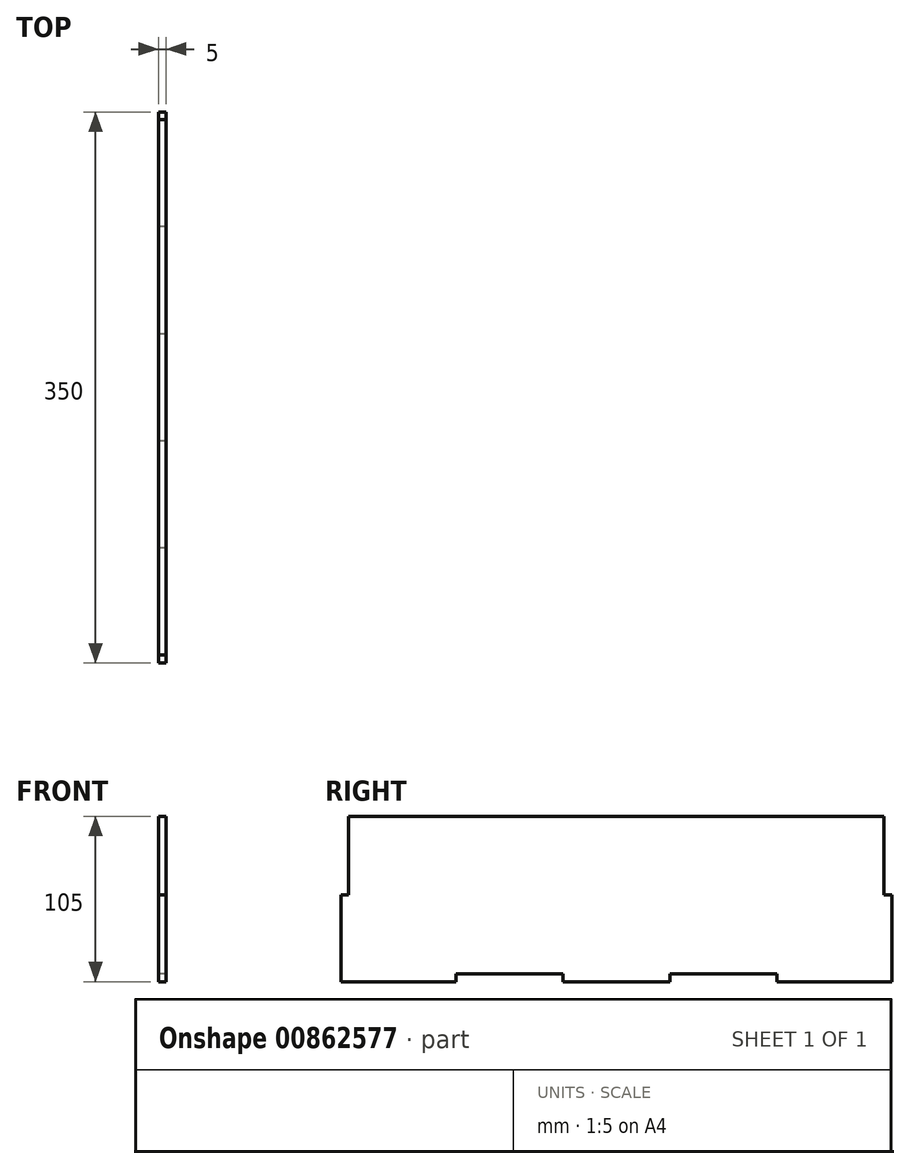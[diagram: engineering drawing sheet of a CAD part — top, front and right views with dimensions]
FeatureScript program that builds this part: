
annotation { "Feature Type Name" : "Feature", "Feature Type Description" : "" }
export const myFeature = defineFeature(function(context is Context, id is Id, definition is map)
    precondition{}
    {
        {
            var Q0;
            Q0=qCreatedBy(makeId("Right.planeOp"),FACE);
            var sketch = newSketch(context, id + "F0", { "sketchPlane" : qUnion([Q0])});
            skLineSegment(sketch, "E0.bottom", {"start": v(175, -50) * mm, "end": v(-175, -50) * mm});
            skLineSegment(sketch, "E0.top", {"start": v(170, 50) * mm, "end": v(-170, 50) * mm});
            skLineSegment(sketch, "E0.left", {"start": v(175, -50) * mm, "end": v(175, 0) * mm});
            skLineSegment(sketch, "E0.right", {"start": v(-175, -50) * mm, "end": v(-175, 0) * mm});
            skPoint(sketch, "E0.middle", {"position": v(0, 0) * mm});
            skLineSegment(sketch, "E1", {"start": v(0, 104.97) * mm, "end": v(0, -112.64) * mm});
            skLineSegment(sketch, "E2", {"start": v(-175, -50) * mm, "end": v(-175, -55) * mm});
            skLineSegment(sketch, "E3", {"start": v(-175, -55) * mm, "end": v(-102, -55) * mm});
            skLineSegment(sketch, "E4", {"start": v(-102, -55) * mm, "end": v(-102, -50) * mm});
            skLineSegment(sketch, "E5", {"start": v(-34, -50) * mm, "end": v(-34, -55) * mm});
            skLineSegment(sketch, "E6", {"start": v(-34, -55) * mm, "end": v(0, -55) * mm});
            skLineSegment(sketch, "E7.MirrorCS", {"start": v(175, -50) * mm, "end": v(175, -55) * mm});
            skLineSegment(sketch, "E8.MirrorCS", {"start": v(175, -55) * mm, "end": v(102, -55) * mm});
            skLineSegment(sketch, "E9.MirrorCS", {"start": v(102, -55) * mm, "end": v(102, -50) * mm});
            skLineSegment(sketch, "E10.MirrorCS", {"start": v(34, -50) * mm, "end": v(34, -55) * mm});
            skLineSegment(sketch, "E11.MirrorCS", {"start": v(34, -55) * mm, "end": v(0, -55) * mm});
            skLineSegment(sketch, "E12", {"start": v(-5, 50) * mm, "end": v(-5, -50) * mm});
            skLineSegment(sketch, "E13.MirrorCS", {"start": v(5, 50) * mm, "end": v(5, -50) * mm});
            skLineSegment(sketch, "E14", {"start": v(-170, 50) * mm, "end": v(-170, 0) * mm});
            skLineSegment(sketch, "E15", {"start": v(-170, 0) * mm, "end": v(-175, 0) * mm});
            skLineSegment(sketch, "E16.MirrorCS", {"start": v(170, 50) * mm, "end": v(170, 0) * mm});
            skLineSegment(sketch, "E17.MirrorCS", {"start": v(170, 0) * mm, "end": v(175, 0) * mm});
            skPoint(sketch, "E18.orphan", {"position": v(-175, 50) * mm});
            skPoint(sketch, "E19.orphan", {"position": v(175, 50) * mm});
            skSolve(sketch);
        }
        {
            var Q0;
            Q0 = qSketchRegion(id + "F0", true);
            extrude(context, id + "F1", {"entities" : qUnion([Q0]), "depth" : 5 * mm, "offsetDistance" : 25 * mm});
        }
    });
